# Revit family: EKF_EE_ПоперечнаяРейкаСпециальнаяFORT_PROxima
name_source: partatom
category: Электрооборудование
units: mm (PartAtom-declared; Revit-internal decimal feet)

## family parameters
Всегда вертикально = Нет
На основе рабочей плоскости = Да
Общий = Да
При загрузке вырезать с полостями = Нет
Размер круглого соединителя = Использовать диаметр
Тип детали = Силовой щит
Точка расчета площади = Нет

## types (4) — shared parameters
ADSK_Единица измерения = шт.
ADSK_Завод-изготовитель = EKF
ADSK_Количество = 1
ADSK_Марка = Поперечная рейка специальная FORT
ADSK_Материал = Сталь_Оцинкованная
ADSK_Обозначение = Поперечная рейка специальная FORT
ADSK_Размер_Высота = 45 мм
ADSK_Размер_Глубина = 33 мм
Изготовитель = EKF
Серия номенклатуры = PROxima
Степень защиты IP = -
ТВ = EKF_2
Тип установки = -
zero-valued in all types: ADSK_Масса, Отметка по умолчанию

## per-type parameters (varying)
| type | ADSK_Код изделия | ADSK_Размер_Ширина | Тип |
| Поперечная рейка специальная FORT для крепления к вертикальным рейкам для корпуса шириной 1000 (4шт.) EKF PROxima | FPR10V | 926 мм | 294 мм |
| Поперечная рейка специальная FORT для крепления к вертикальным рейкам для корпуса шириной 400 (4шт.) EKF PROxima | FPR4V | 326 мм | 295 мм |
| Поперечная рейка специальная FORT для крепления к вертикальным рейкам для корпуса шириной 600 (4шт.) EKF PROxima | FPR6V | 526 мм | 296 мм |
| Поперечная рейка специальная FORT для крепления к вертикальным рейкам для корпуса шириной 800 (4шт.) EKF PROxima | FPR8V | 726 мм | 297 мм |

note: column(s) folded — value = type name in every type: ADSK_Наименование
